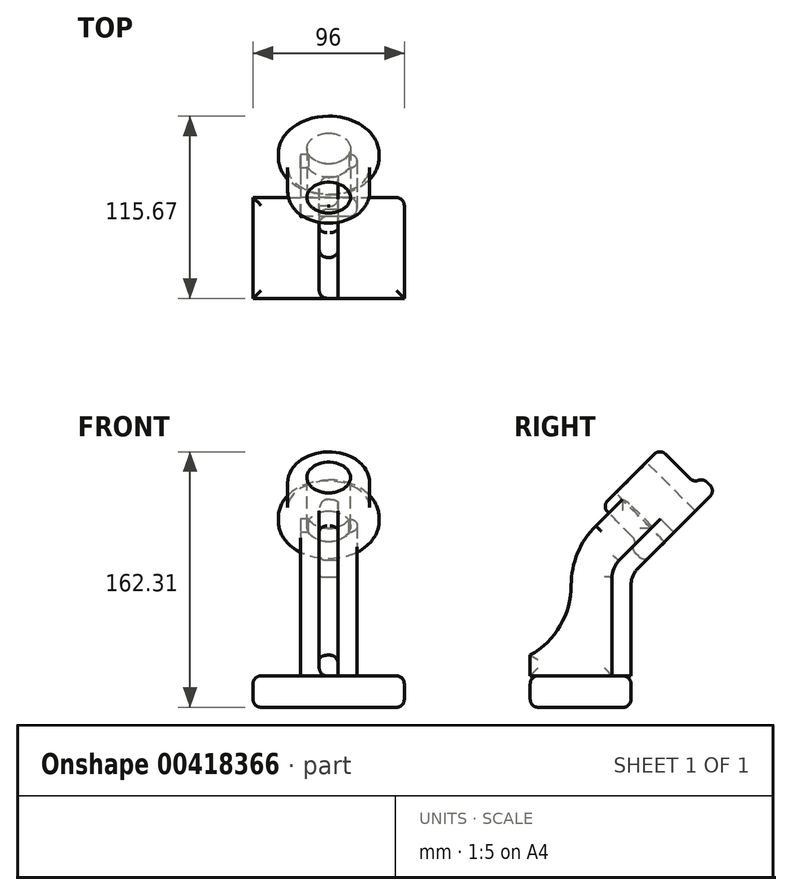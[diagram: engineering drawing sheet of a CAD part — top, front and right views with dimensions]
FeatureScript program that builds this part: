
annotation { "Feature Type Name" : "Feature", "Feature Type Description" : "" }
export const myFeature = defineFeature(function(context is Context, id is Id, definition is map)
    precondition{}
    {
        {
            var Q0;
            Q0=qCreatedBy(makeId("Top.planeOp"),FACE);
            var sketch = newSketch(context, id + "F0", { "sketchPlane" : qUnion([Q0])});
            skLineSegment(sketch, "E0.bottom", {"start": v(-48, 0) * mm, "end": v(48, 0) * mm});
            skLineSegment(sketch, "E0.top", {"start": v(-48, -64) * mm, "end": v(48, -64) * mm});
            skLineSegment(sketch, "E0.left", {"start": v(-48, 0) * mm, "end": v(-48, -64) * mm});
            skLineSegment(sketch, "E0.right", {"start": v(48, 0) * mm, "end": v(48, -64) * mm});
            skSolve(sketch);
        }
        {
            var Q0;
            Q0=makeQuery(id+"F0.imprint","IMPRINT",FACE,{"disambiguationData":[TD([[makeQuery(id+"F0.imprint","IMPRINT",EDGE,{"derivedFrom":sQuery(id+"F0.wireOp",EDGE,"E0.bottom")}),-1.0]])]});
            extrude(context, id + "F1", {"entities" : qUnion([Q0]), "depth" : 20 * mm});
        }
        {
            var Q0;
            Q0=qCreatedBy(makeId("Right.planeOp"),FACE);
            var sketch = newSketch(context, id + "F2", { "sketchPlane" : qUnion([Q0])});
            skLineSegment(sketch, "E1", {"start": v(0, 0) * mm, "end": v(2.39, 3.1) * mm, "construction": true});
            skLineSegment(sketch, "E2", {"start": v(0, 146) * mm, "end": v(0, 0) * mm, "construction": true});
            skLineSegment(sketch, "E3", {"start": v(0, 146) * mm, "end": v(-18.38, 127.62) * mm});
            skLineSegment(sketch, "E4", {"start": v(-18.38, 127.62) * mm, "end": v(4.24, 104.99) * mm});
            skLineSegment(sketch, "E5", {"start": v(4.24, 104.99) * mm, "end": v(0, 100.75) * mm});
            skLineSegment(sketch, "E6", {"start": v(0, 100.75) * mm, "end": v(8.49, 92.26) * mm});
            skLineSegment(sketch, "E7", {"start": v(8.49, 92.26) * mm, "end": v(31.11, 114.89) * mm});
            skLineSegment(sketch, "E8", {"start": v(0, 146) * mm, "end": v(31.11, 114.89) * mm});
            skSolve(sketch);
        }
        {
            var Q0;
            Q0=makeQuery(id+"F2.imprint","IMPRINT",FACE,{"disambiguationData":[TD([[makeQuery(id+"F2.imprint","IMPRINT",EDGE,{"derivedFrom":sQuery(id+"F2.wireOp",EDGE,"E3")}),1.0]])]});
            var Q1;
            Q1=sQuery(id+"F2.wireOp",EDGE,"E8");
            revolve(context, id + "F3", {"entities" : qUnion([Q0]), "axis" : qUnion([Q1]), "revolveType" : RevolveType.FULL});
        }
        {
            var Q0;
            Q0=qCreatedBy(makeId("Right.planeOp"),FACE);
            var sketch = newSketch(context, id + "F4", { "sketchPlane" : qUnion([Q0])});
            skLineSegment(sketch, "E9", {"start": v(45.25, 146) * mm, "end": v(53.74, 137.51) * mm, "construction": true});
            skLineSegment(sketch, "E10.0", {"start": v(0, 100.75) * mm, "end": v(45.25, 146) * mm, "construction": true});
            skLineSegment(sketch, "E11", {"start": v(0, 0) * mm, "end": v(0, 77.56) * mm});
            skLineSegment(sketch, "E12.0.0", {"start": v(-64, 0) * mm, "end": v(0, 0) * mm, "construction": true});
            skLineSegment(sketch, "E12.0.1", {"start": v(0, 0) * mm, "end": v(0, 20) * mm, "construction": true});
            skLineSegment(sketch, "E12.0.2", {"start": v(0, 20) * mm, "end": v(-64, 20) * mm, "construction": true});
            skLineSegment(sketch, "E12.0.3", {"start": v(-64, 20) * mm, "end": v(-64, 0) * mm, "construction": true});
            skLineSegment(sketch, "E13", {"start": v(-12, 20) * mm, "end": v(-12, 82.53) * mm});
            skLineSegment(sketch, "E14", {"start": v(53.74, 137.51) * mm, "end": v(4.4, 88.17) * mm});
            skLineSegment(sketch, "E15", {"start": v(45.25, 146) * mm, "end": v(-7.6, 93.14) * mm});
            skArc(sketch, "E16.filletArc", {"start": v(4.4, 88.17) * mm, "mid": v(1.14, 83.3) * mm, "end": v(0, 77.56) * mm});
            skArc(sketch, "E17.filletArc", {"start": v(-7.6, 93.14) * mm, "mid": v(-10.86, 88.27) * mm, "end": v(-12, 82.53) * mm});
            skLineSegment(sketch, "E18", {"start": v(15, 77.56) * mm, "end": v(-97.57, 77.56) * mm, "construction": true});
            skLineSegment(sketch, "E19", {"start": v(-12, 20) * mm, "end": v(0, 20) * mm});
            skLineSegment(sketch, "E20", {"start": v(0, 100.75) * mm, "end": v(18.82, 119.57) * mm});
            skLineSegment(sketch, "E21", {"start": v(18.82, 119.57) * mm, "end": v(27.3, 111.08) * mm});
            skLineSegment(sketch, "E22", {"start": v(27.3, 111.08) * mm, "end": v(4.4, 88.17) * mm});
            skSolve(sketch);
        }
        {
            var Q0;
            Q0=makeQuery(id+"F4.imprint","IMPRINT",FACE,{"disambiguationData":[TD([[makeQuery(id+"F4.imprint","IMPRINT",EDGE,{"derivedFrom":sQuery(id+"F4.wireOp",EDGE,"E13")}),-1.0]])]});
            extrude(context, id + "F5", {"entities" : qUnion([Q0]), "depth" : 18 * mm, "hasSecondDirection" : true, "secondDirectionOppositeDirection" : true, "secondDirectionDepth" : 18 * mm});
        }
        {
            var Q0;
            Q0=qCreatedBy(makeId("Right.planeOp"),FACE);
            var sketch = newSketch(context, id + "F6", { "sketchPlane" : qUnion([Q0])});
            skLineSegment(sketch, "E23", {"start": v(18.38, 164.38) * mm, "end": v(41.01, 141.76) * mm, "construction": true});
            skLineSegment(sketch, "E24", {"start": v(4.24, 104.99) * mm, "end": v(-18.38, 127.62) * mm, "construction": true});
            skLineSegment(sketch, "E25.0.0", {"start": v(27.3, 111.08) * mm, "end": v(18.82, 119.57) * mm, "construction": true});
            skLineSegment(sketch, "E25.0.1", {"start": v(18.82, 119.57) * mm, "end": v(-7.6, 93.14) * mm, "construction": true});
            skArc(sketch, "E25.0.2", {"start": v(-7.6, 93.14) * mm, "mid": v(-10.86, 88.27) * mm, "end": v(-12, 82.53) * mm, "construction": true});
            skLineSegment(sketch, "E25.0.3", {"start": v(-12, 82.53) * mm, "end": v(-12, 20) * mm, "construction": true});
            skLineSegment(sketch, "E25.0.4", {"start": v(-12, 20) * mm, "end": v(0, 20) * mm, "construction": true});
            skLineSegment(sketch, "E25.0.5", {"start": v(0, 20) * mm, "end": v(0, 77.56) * mm, "construction": true});
            skArc(sketch, "E25.0.6", {"start": v(0, 77.56) * mm, "mid": v(1.14, 83.3) * mm, "end": v(4.4, 88.17) * mm, "construction": true});
            skLineSegment(sketch, "E25.0.7", {"start": v(4.4, 88.17) * mm, "end": v(27.3, 111.08) * mm, "construction": true});
            skLineSegment(sketch, "E26.0.0", {"start": v(-64, 0) * mm, "end": v(0, 0) * mm, "construction": true});
            skLineSegment(sketch, "E26.0.1", {"start": v(0, 0) * mm, "end": v(0, 20) * mm, "construction": true});
            skLineSegment(sketch, "E26.0.2", {"start": v(0, 20) * mm, "end": v(-64, 20) * mm, "construction": true});
            skLineSegment(sketch, "E26.0.3", {"start": v(-64, 20) * mm, "end": v(-64, 0) * mm, "construction": true});
            skLineSegment(sketch, "E27", {"start": v(-39.29, 98.23) * mm, "end": v(29.7, 167.21) * mm, "construction": true});
            skPoint(sketch, "E27.endSnap0", {"position": v(29.7, 153.07) * mm});
            skLineSegment(sketch, "E28", {"start": v(15, 77.56) * mm, "end": v(-179.75, 77.56) * mm, "construction": true});
            skArc(sketch, "E29", {"start": v(-22.3, 115.22) * mm, "mid": v(-33.92, 97.96) * mm, "end": v(-38, 77.56) * mm});
            skLineSegment(sketch, "E30", {"start": v(-64, 20) * mm, "end": v(-64, 49.96) * mm, "construction": true});
            skArc(sketch, "E31", {"start": v(-38, 77.56) * mm, "mid": v(-44.98, 51.82) * mm, "end": v(-64, 33.13) * mm});
            skLineSegment(sketch, "E32", {"start": v(-64, 33.13) * mm, "end": v(-64, 20) * mm});
            skLineSegment(sketch, "E33", {"start": v(-12, 20) * mm, "end": v(-12, 82.53) * mm});
            skArc(sketch, "E34", {"start": v(-12, 82.53) * mm, "mid": v(-10.36, 88.07) * mm, "end": v(-7.6, 93.14) * mm});
            skLineSegment(sketch, "E35", {"start": v(-7.6, 93.14) * mm, "end": v(18.82, 119.57) * mm});
            skLineSegment(sketch, "E36", {"start": v(18.82, 119.57) * mm, "end": v(0.44, 137.95) * mm});
            skLineSegment(sketch, "E37", {"start": v(0.44, 137.95) * mm, "end": v(-22.3, 115.22) * mm});
            skLineSegment(sketch, "E38", {"start": v(-64, 20) * mm, "end": v(-12, 20) * mm});
            skSolve(sketch);
        }
        {
            var Q0;
            Q0=makeQuery(id+"F6.imprint","IMPRINT",FACE,{"disambiguationData":[TD([[makeQuery(id+"F6.imprint","IMPRINT",EDGE,{"derivedFrom":sQuery(id+"F6.wireOp",EDGE,"E29")}),1.0]])]});
            extrude(context, id + "F7", {"entities" : qUnion([Q0]), "depth" : 6 * mm, "hasSecondDirection" : true, "secondDirectionOppositeDirection" : true, "secondDirectionDepth" : 6 * mm});
        }
        {
            var Q0;
            Q0=makeQuery(id+"F3.opRevolve","SWEPT_FACE",FACE,{"disambiguationData":[OSD([sQuery(id+"F2.wireOp",EDGE,"E3")])]});
            var sketch = newSketch(context, id + "F8", { "sketchPlane" : qUnion([Q0])});
            skCircle(sketch, "E39.0.0", {"center": v(0, 103.24) * mm, "radius": 26 * mm});
            skCircle(sketch, "E40", {"center": v(0, 103.24) * mm, "radius": 13.84 * mm});
            skSolve(sketch);
        }
        {
            var Q0;
            Q0=makeQuery(id+"F8.imprint","IMPRINT",FACE,{"disambiguationData":[TD([[makeQuery(id+"F8.imprint","IMPRINT",EDGE,{"derivedFrom":sQuery(id+"F8.wireOp",EDGE,"E40")}),1.0]])]});
            extrude(context, id + "F9", {"entities" : qUnion([Q0]), "operationType" : NewBodyOperationType.REMOVE, "oppositeDirection" : true, "depth" : 50.5 * mm});
        }
        {
            var Q0;
            Q0=makeQuery(id+"F3.opRevolve","SWEPT_FACE",FACE,{"disambiguationData":[OSD([sQuery(id+"F2.wireOp",EDGE,"E4")])]});
            var Q1;
            Q1=makeQuery(id+"F7.opExtrude","CAP_FACE",FACE,{"disambiguationData":[OSD([sQuery(id+"F6.wireOp",EDGE,"E29"),sQuery(id+"F6.wireOp",EDGE,"E31"),sQuery(id+"F6.wireOp",EDGE,"E32"),sQuery(id+"F6.wireOp",EDGE,"E33"),sQuery(id+"F6.wireOp",EDGE,"E34"),sQuery(id+"F6.wireOp",EDGE,"E35"),sQuery(id+"F6.wireOp",EDGE,"E36"),sQuery(id+"F6.wireOp",EDGE,"E37"),sQuery(id+"F6.wireOp",EDGE,"E38")])],"isStart":true});
            fillet(context, id + "F10", {"entities" : qUnion([Q0, Q1]), "radius" : 5 * mm, "tangentPropagation" : true, "allowEdgeOverflow" : false});
        }
        {
            var Q0;
            Q0=makeQuery(id+"F1.opExtrude","SWEPT_EDGE",EDGE,{"disambiguationData":[OSD([sQuery(id+"F0.wireOp",EDGE,"E0.bottom"),sQuery(id+"F0.wireOp",EDGE,"E0.right")])]});
            var Q1;
            Q1=makeQuery(id+"F1.opExtrude","CAP_FACE",FACE,{"disambiguationData":[OSD([sQuery(id+"F0.wireOp",EDGE,"E0.bottom"),sQuery(id+"F0.wireOp",EDGE,"E0.top"),sQuery(id+"F0.wireOp",EDGE,"E0.left"),sQuery(id+"F0.wireOp",EDGE,"E0.right")])],"isStart":false});
            var Q2;
            Q2=makeQuery(id+"F1.opExtrude","CAP_FACE",FACE,{"disambiguationData":[OSD([sQuery(id+"F0.wireOp",EDGE,"E0.bottom"),sQuery(id+"F0.wireOp",EDGE,"E0.top"),sQuery(id+"F0.wireOp",EDGE,"E0.left"),sQuery(id+"F0.wireOp",EDGE,"E0.right")])],"isStart":true});
            var Q3;
            Q3=makeQuery(id+"F7.opExtrude","CAP_EDGE",EDGE,{"disambiguationData":[OSD([sQuery(id+"F6.wireOp",EDGE,"E31")])],"isStart":false});
            var Q4;
            Q4=makeQuery(id+"F5.opExtrude","CAP_EDGE",EDGE,{"disambiguationData":[OSD([sQuery(id+"F4.wireOp",EDGE,"E11")])],"isStart":false});
            var Q5;
            Q5=makeQuery(id+"F5.opExtrude","CAP_EDGE",EDGE,{"disambiguationData":[OSD([sQuery(id+"F4.wireOp",EDGE,"E17.filletArc")])],"isStart":false});
            var Q6;
            Q6=makeQuery(id+"F3.opRevolve","SWEPT_FACE",FACE,{"disambiguationData":[OSD([sQuery(id+"F2.wireOp",EDGE,"E6")])]});
            fillet(context, id + "F11", {"entities" : qUnion([Q0, Q1, Q2, Q3, Q4, Q5, Q6]), "radius" : 5 * mm, "tangentPropagation" : true, "allowEdgeOverflow" : false});
        }
    });
